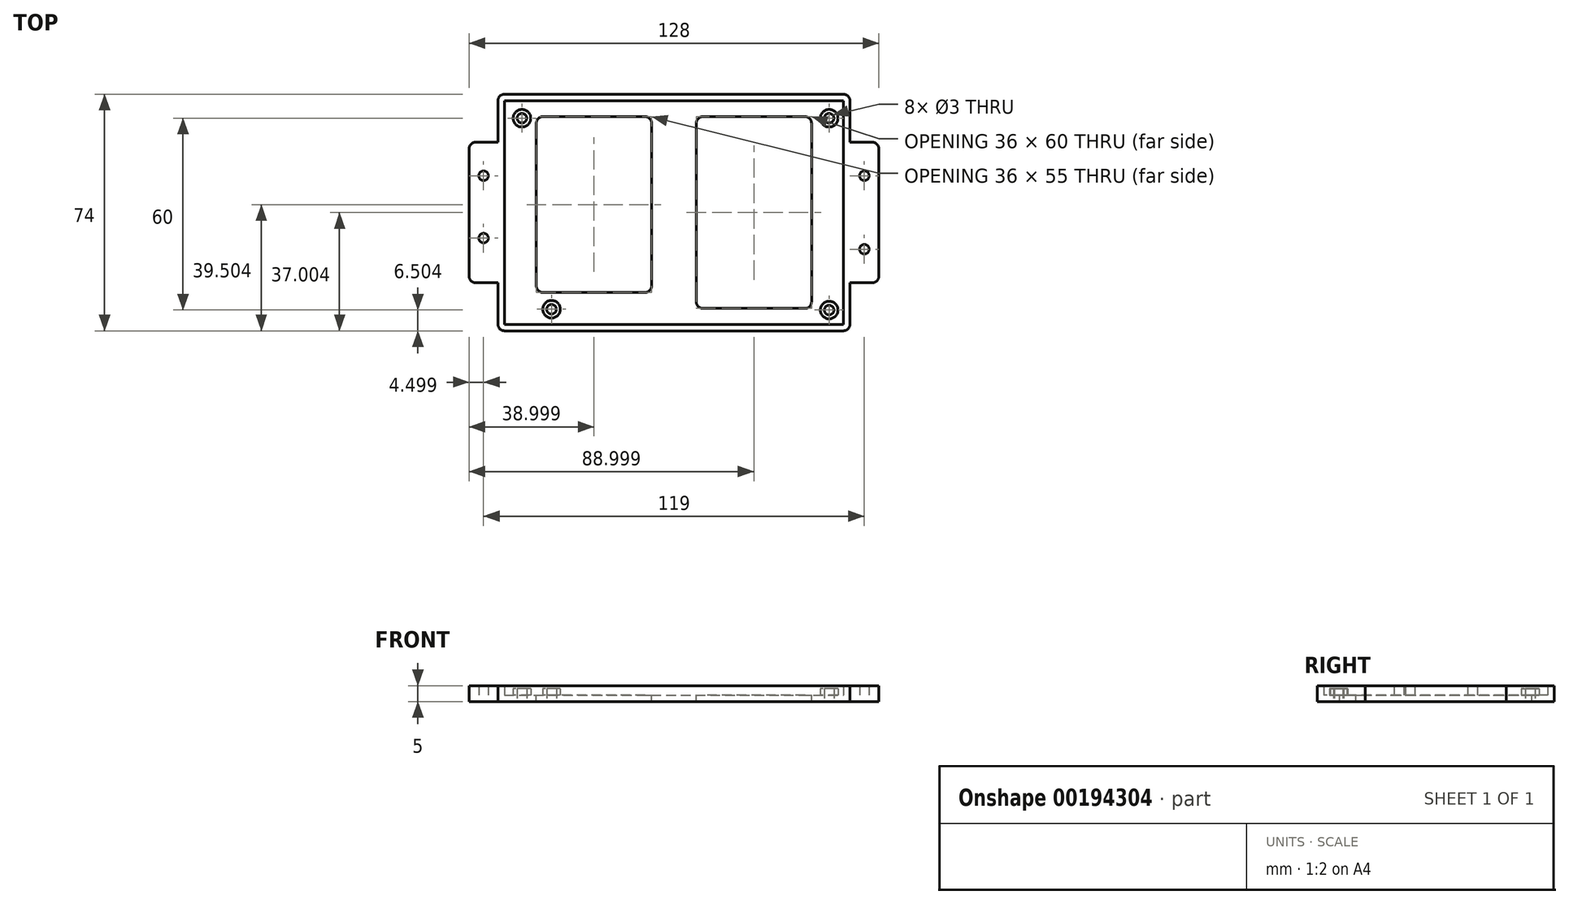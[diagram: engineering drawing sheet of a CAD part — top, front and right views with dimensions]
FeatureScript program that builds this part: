
annotation { "Feature Type Name" : "Feature", "Feature Type Description" : "" }
export const myFeature = defineFeature(function(context is Context, id is Id, definition is map)
    precondition{}
    {
        {
            var Q0;
            Q0=qCreatedBy(makeId("Top.planeOp"),FACE);
            var sketch = newSketch(context, id + "F0", { "sketchPlane" : qUnion([Q0])});
            skLineSegment(sketch, "E0.bottom", {"start": v(-53.24, 37.4) * mm, "end": v(52.76, 37.4) * mm});
            skLineSegment(sketch, "E0.top", {"start": v(-53.24, -32.6) * mm, "end": v(52.76, -32.6) * mm});
            skLineSegment(sketch, "E0.left", {"start": v(-53.24, 37.4) * mm, "end": v(-53.24, -32.6) * mm});
            skLineSegment(sketch, "E0.right", {"start": v(52.76, 37.4) * mm, "end": v(52.76, -32.6) * mm});
            skCircle(sketch, "E1", {"center": v(-38.5, -27.85) * mm, "radius": 1.5 * mm});
            skCircle(sketch, "E2", {"center": v(-47.74, 31.9) * mm, "radius": 1.5 * mm});
            skCircle(sketch, "E3", {"center": v(48.26, 31.9) * mm, "radius": 1.5 * mm});
            skCircle(sketch, "E4", {"center": v(48.26, -28.1) * mm, "radius": 1.5 * mm});
            skLineSegment(sketch, "E5.0", {"start": v(-55.24, 37.4) * mm, "end": v(-55.24, -32.6) * mm});
            skLineSegment(sketch, "E5.1", {"start": v(-53.24, 39.4) * mm, "end": v(52.76, 39.4) * mm});
            skLineSegment(sketch, "E5.2", {"start": v(54.76, 37.4) * mm, "end": v(54.76, -32.6) * mm});
            skLineSegment(sketch, "E5.3", {"start": v(-53.24, -34.6) * mm, "end": v(52.76, -34.6) * mm});
            skPoint(sketch, "E6.visualSharp", {"position": v(-55.24, 39.4) * mm});
            skArc(sketch, "E6.filletArc", {"start": v(-53.24, 39.4) * mm, "mid": v(-54.66, 38.82) * mm, "end": v(-55.24, 37.4) * mm});
            skPoint(sketch, "E7.visualSharp", {"position": v(-55.24, -34.6) * mm});
            skArc(sketch, "E7.filletArc", {"start": v(-55.24, -32.6) * mm, "mid": v(-54.66, -34.01) * mm, "end": v(-53.24, -34.6) * mm});
            skPoint(sketch, "E8.visualSharp", {"position": v(54.76, -34.6) * mm});
            skArc(sketch, "E8.filletArc", {"start": v(52.76, -34.6) * mm, "mid": v(54.17, -34.01) * mm, "end": v(54.76, -32.6) * mm});
            skPoint(sketch, "E9.visualSharp", {"position": v(54.76, 39.4) * mm});
            skArc(sketch, "E9.filletArc", {"start": v(54.76, 37.4) * mm, "mid": v(54.17, 38.82) * mm, "end": v(52.76, 39.4) * mm});
            skLineSegment(sketch, "E10.bottom", {"start": v(-55.24, 24.4) * mm, "end": v(-64.24, 24.4) * mm});
            skLineSegment(sketch, "E10.top", {"start": v(-55.24, -19.6) * mm, "end": v(-64.24, -19.6) * mm});
            skLineSegment(sketch, "E10.left", {"start": v(-55.24, 24.4) * mm, "end": v(-55.24, -19.6) * mm});
            skLineSegment(sketch, "E10.right", {"start": v(-64.24, 24.4) * mm, "end": v(-64.24, -19.6) * mm});
            skLineSegment(sketch, "E11.bottom", {"start": v(54.76, 24.4) * mm, "end": v(63.76, 24.4) * mm});
            skLineSegment(sketch, "E11.top", {"start": v(54.76, -19.6) * mm, "end": v(63.76, -19.6) * mm});
            skLineSegment(sketch, "E11.left", {"start": v(54.76, 24.4) * mm, "end": v(54.76, -19.6) * mm});
            skLineSegment(sketch, "E11.right", {"start": v(63.76, 24.4) * mm, "end": v(63.76, -19.6) * mm});
            skPoint(sketch, "E12", {"position": v(-59.7, 0) * mm});
            skPoint(sketch, "E13", {"position": v(59.26, 0) * mm});
            skCircle(sketch, "E14", {"center": v(-59.74, 13.9) * mm, "radius": 1.5 * mm});
            skCircle(sketch, "E15", {"center": v(-59.74, -5.6) * mm, "radius": 1.5 * mm});
            skCircle(sketch, "E16", {"center": v(59.26, 13.9) * mm, "radius": 1.5 * mm});
            skCircle(sketch, "E17", {"center": v(59.26, -9.1) * mm, "radius": 1.5 * mm});
            skCircle(sketch, "E18.0", {"center": v(-47.74, 31.9) * mm, "radius": 2.75 * mm});
            skCircle(sketch, "E19.0", {"center": v(48.26, 31.9) * mm, "radius": 2.75 * mm});
            skCircle(sketch, "E20.0", {"center": v(48.26, -28.1) * mm, "radius": 2.75 * mm});
            skCircle(sketch, "E21.0", {"center": v(-38.5, -27.85) * mm, "radius": 2.75 * mm});
            skSolve(sketch);
        }
        {
            var Q0;
            Q0=makeQuery(id+"F0.imprint","IMPRINT",FACE,{"disambiguationData":[TD([[makeQuery(id+"F0.imprint","IMPRINT",EDGE,{"derivedFrom":sQuery(id+"F0.wireOp",EDGE,"E0.bottom")}),-1.0]])]});
            extrude(context, id + "F1", {"entities" : qUnion([Q0]), "depth" : 2 * mm});
        }
        {
            var Q0;
            Q0=makeQuery(id+"F0.imprint","IMPRINT",FACE,{"disambiguationData":[TD([[makeQuery(id+"F0.imprint","IMPRINT",EDGE,{"derivedFrom":sQuery(id+"F0.wireOp",EDGE,"E2")}),-1.0]])]});
            var Q1;
            Q1=makeQuery(id+"F0.imprint","IMPRINT",FACE,{"disambiguationData":[TD([[makeQuery(id+"F0.imprint","IMPRINT",EDGE,{"derivedFrom":sQuery(id+"F0.wireOp",EDGE,"E1")}),-1.0]])]});
            var Q2;
            Q2=makeQuery(id+"F0.imprint","IMPRINT",FACE,{"disambiguationData":[TD([[makeQuery(id+"F0.imprint","IMPRINT",EDGE,{"derivedFrom":sQuery(id+"F0.wireOp",EDGE,"E4")}),-1.0]])]});
            var Q3;
            Q3=makeQuery(id+"F0.imprint","IMPRINT",FACE,{"disambiguationData":[TD([[makeQuery(id+"F0.imprint","IMPRINT",EDGE,{"derivedFrom":sQuery(id+"F0.wireOp",EDGE,"E3")}),-1.0]])]});
            extrude(context, id + "F2", {"entities" : qUnion([Q0, Q1, Q2, Q3]), "operationType" : NewBodyOperationType.ADD, "depth" : 4 * mm});
        }
        {
            var Q0;
            Q0=makeQuery(id+"F0.imprint","IMPRINT",FACE,{"disambiguationData":[TD([[makeQuery(id+"F0.imprint","IMPRINT",EDGE,{"derivedFrom":sQuery(id+"F0.wireOp",EDGE,"E10.bottom")}),1.0]])]});
            var Q1;
            Q1=makeQuery(id+"F0.imprint","IMPRINT",FACE,{"disambiguationData":[TD([[makeQuery(id+"F0.imprint","IMPRINT",EDGE,{"derivedFrom":sQuery(id+"F0.wireOp",EDGE,"E0.bottom")}),1.0]])]});
            var Q2;
            Q2=makeQuery(id+"F0.imprint","IMPRINT",FACE,{"disambiguationData":[TD([[makeQuery(id+"F0.imprint","IMPRINT",EDGE,{"derivedFrom":sQuery(id+"F0.wireOp",EDGE,"E11.bottom")}),-1.0]])]});
            extrude(context, id + "F3", {"entities" : qUnion([Q0, Q1, Q2]), "operationType" : NewBodyOperationType.ADD, "depth" : 5 * mm});
        }
        {
            var Q0;
            Q0=makeQuery(id+"F3.opExtrude","SWEPT_EDGE",EDGE,{"disambiguationData":[OSD([sQuery(id+"F0.wireOp",EDGE,"E10.bottom"),sQuery(id+"F0.wireOp",EDGE,"E10.right")])]});
            var Q1;
            Q1=makeQuery(id+"F3.opExtrude","SWEPT_EDGE",EDGE,{"disambiguationData":[OSD([sQuery(id+"F0.wireOp",EDGE,"E10.top"),sQuery(id+"F0.wireOp",EDGE,"E10.right")])]});
            var Q2;
            Q2=makeQuery(id+"F3.opExtrude","SWEPT_EDGE",EDGE,{"disambiguationData":[OSD([sQuery(id+"F0.wireOp",EDGE,"E11.top"),sQuery(id+"F0.wireOp",EDGE,"E11.right")])]});
            var Q3;
            Q3=makeQuery(id+"F3.opExtrude","SWEPT_EDGE",EDGE,{"disambiguationData":[OSD([sQuery(id+"F0.wireOp",EDGE,"E11.bottom"),sQuery(id+"F0.wireOp",EDGE,"E11.right")])]});
            fillet(context, id + "F4", {"entities" : qUnion([Q0, Q1, Q2, Q3]), "radius" : 2 * mm, "tangentPropagation" : true, "allowEdgeOverflow" : false});
        }
        {
            var Q0;
            Q0=makeQuery(id+"F1.opExtrude","CAP_FACE",FACE,{"disambiguationData":[OSD([sQuery(id+"F0.wireOp",EDGE,"E0.bottom"),sQuery(id+"F0.wireOp",EDGE,"E0.top"),sQuery(id+"F0.wireOp",EDGE,"E0.left"),sQuery(id+"F0.wireOp",EDGE,"E0.right"),sQuery(id+"F0.wireOp",EDGE,"E18.0"),sQuery(id+"F0.wireOp",EDGE,"E19.0"),sQuery(id+"F0.wireOp",EDGE,"E20.0"),sQuery(id+"F0.wireOp",EDGE,"E21.0")])],"isStart":false});
            var sketch = newSketch(context, id + "F5", { "sketchPlane" : qUnion([Q0])});
            skLineSegment(sketch, "E22.bottom", {"start": v(40.76, -27.6) * mm, "end": v(8.76, -27.6) * mm});
            skLineSegment(sketch, "E22.top", {"start": v(40.76, 32.4) * mm, "end": v(8.76, 32.4) * mm});
            skLineSegment(sketch, "E22.left", {"start": v(42.76, -25.6) * mm, "end": v(42.76, 30.4) * mm});
            skLineSegment(sketch, "E22.right", {"start": v(6.76, -25.6) * mm, "end": v(6.76, 30.4) * mm});
            skLineSegment(sketch, "E23.bottom", {"start": v(-9.24, -22.6) * mm, "end": v(-41.24, -22.6) * mm});
            skLineSegment(sketch, "E23.top", {"start": v(-9.24, 32.4) * mm, "end": v(-41.24, 32.4) * mm});
            skLineSegment(sketch, "E23.left", {"start": v(-7.24, -20.6) * mm, "end": v(-7.24, 30.4) * mm});
            skLineSegment(sketch, "E23.right", {"start": v(-43.24, -20.6) * mm, "end": v(-43.24, 30.4) * mm});
            skPoint(sketch, "E24.visualSharp", {"position": v(42.76, -27.6) * mm});
            skArc(sketch, "E24.filletArc", {"start": v(40.76, -27.6) * mm, "mid": v(42.17, -27.01) * mm, "end": v(42.76, -25.6) * mm});
            skPoint(sketch, "E25.visualSharp", {"position": v(42.76, 32.4) * mm});
            skArc(sketch, "E25.filletArc", {"start": v(42.76, 30.4) * mm, "mid": v(42.17, 31.82) * mm, "end": v(40.76, 32.4) * mm});
            skPoint(sketch, "E26.visualSharp", {"position": v(6.76, 32.4) * mm});
            skArc(sketch, "E26.filletArc", {"start": v(8.76, 32.4) * mm, "mid": v(7.34, 31.82) * mm, "end": v(6.76, 30.4) * mm});
            skPoint(sketch, "E27.visualSharp", {"position": v(6.76, -27.6) * mm});
            skArc(sketch, "E27.filletArc", {"start": v(6.76, -25.6) * mm, "mid": v(7.34, -27.01) * mm, "end": v(8.76, -27.6) * mm});
            skPoint(sketch, "E28.visualSharp", {"position": v(-7.24, -22.6) * mm});
            skArc(sketch, "E28.filletArc", {"start": v(-9.24, -22.6) * mm, "mid": v(-7.83, -22.01) * mm, "end": v(-7.24, -20.6) * mm});
            skPoint(sketch, "E29.visualSharp", {"position": v(-7.24, 32.4) * mm});
            skArc(sketch, "E29.filletArc", {"start": v(-7.24, 30.4) * mm, "mid": v(-7.83, 31.82) * mm, "end": v(-9.24, 32.4) * mm});
            skPoint(sketch, "E30.visualSharp", {"position": v(-43.24, 32.4) * mm});
            skArc(sketch, "E30.filletArc", {"start": v(-41.24, 32.4) * mm, "mid": v(-42.66, 31.82) * mm, "end": v(-43.24, 30.4) * mm});
            skPoint(sketch, "E31.visualSharp", {"position": v(-43.24, -22.6) * mm});
            skArc(sketch, "E31.filletArc", {"start": v(-43.24, -20.6) * mm, "mid": v(-42.66, -22.01) * mm, "end": v(-41.24, -22.6) * mm});
            skSolve(sketch);
        }
        {
            var Q0;
            Q0=makeQuery(id+"F5.imprint","IMPRINT",FACE,{"disambiguationData":[TD([[makeQuery(id+"F5.imprint","IMPRINT",EDGE,{"derivedFrom":sQuery(id+"F5.wireOp",EDGE,"E22.bottom")}),-1.0]])]});
            var Q1;
            Q1=makeQuery(id+"F5.imprint","IMPRINT",FACE,{"disambiguationData":[TD([[makeQuery(id+"F5.imprint","IMPRINT",EDGE,{"derivedFrom":sQuery(id+"F5.wireOp",EDGE,"E23.bottom")}),-1.0]])]});
            extrude(context, id + "F6", {"entities" : qUnion([Q0, Q1]), "operationType" : NewBodyOperationType.REMOVE, "oppositeDirection" : true, "depth" : 2 * mm});
        }
    });
